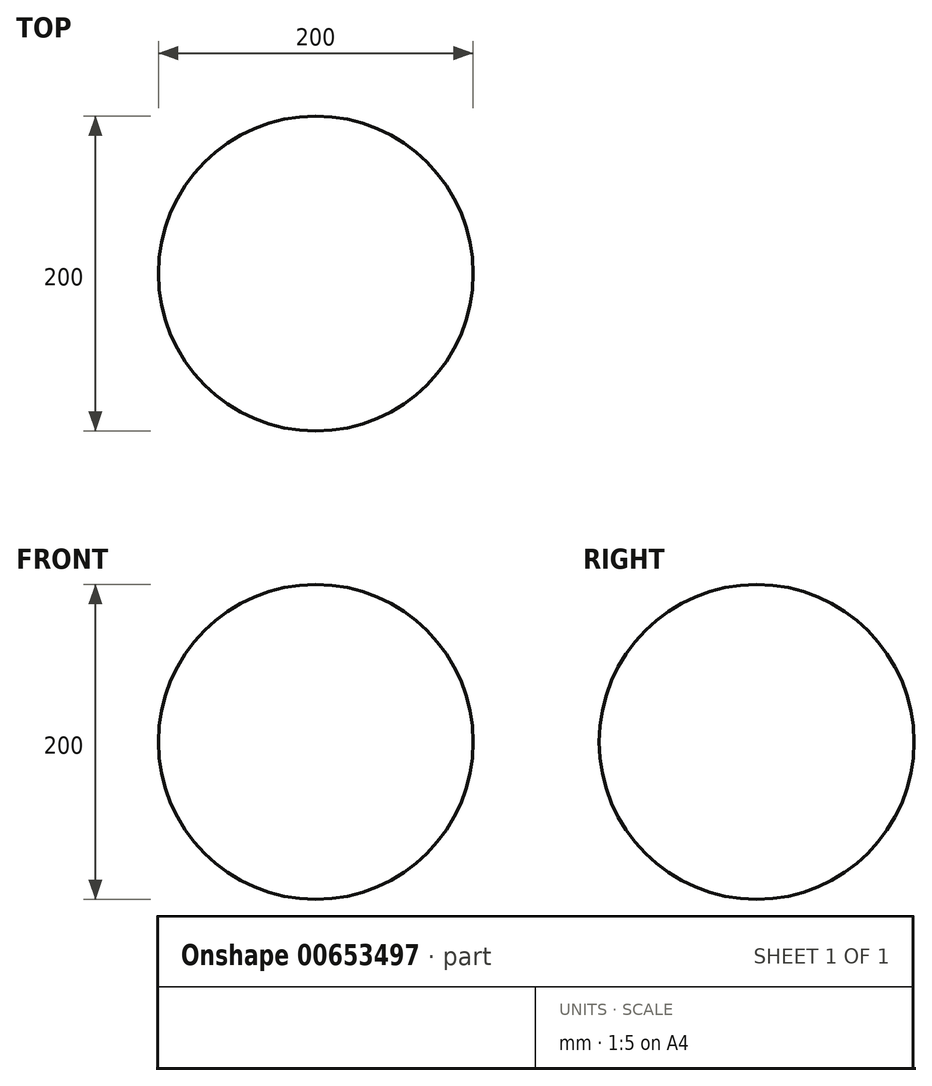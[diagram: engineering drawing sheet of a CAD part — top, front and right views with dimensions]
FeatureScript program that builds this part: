
annotation { "Feature Type Name" : "Feature", "Feature Type Description" : "" }
export const myFeature = defineFeature(function(context is Context, id is Id, definition is map)
    precondition{}
    {
        {
            var Q0;
            Q0=qCreatedBy(makeId("Front.planeOp"),FACE);
            var sketch = newSketch(context, id + "F0", { "sketchPlane" : qUnion([Q0])});
            skLineSegment(sketch, "E0.bottom", {"start": v(100, 100) * mm, "end": v(-100, 100) * mm});
            skLineSegment(sketch, "E0.top", {"start": v(100, -100) * mm, "end": v(-100, -100) * mm});
            skLineSegment(sketch, "E0.left", {"start": v(100, 100) * mm, "end": v(100, -100) * mm});
            skLineSegment(sketch, "E0.right", {"start": v(-100, 100) * mm, "end": v(-100, -100) * mm});
            skPoint(sketch, "E0.middle", {"position": v(0, 0) * mm});
            skSolve(sketch);
        }
        {
            var Q0;
            Q0=makeQuery(id+"F0.imprint","IMPRINT",FACE,{"disambiguationData":[TD([[makeQuery(id+"F0.imprint","IMPRINT",EDGE,{"derivedFrom":sQuery(id+"F0.wireOp",EDGE,"E0.bottom")}),1.0]])]});
            extrude(context, id + "F1", {"entities" : qUnion([Q0]), "depth" : 200 * mm, "offsetDistance" : 25 * mm});
        }
        {
            var Q0;
            Q0=makeQuery(id+"F1.opExtrude","SWEPT_FACE",FACE,{"disambiguationData":[OSD([sQuery(id+"F0.wireOp",EDGE,"E0.left")])]});
            var Q1;
            Q1=makeQuery(id+"F1.opExtrude","CAP_FACE",FACE,{"disambiguationData":[OSD([sQuery(id+"F0.wireOp",EDGE,"E0.bottom"),sQuery(id+"F0.wireOp",EDGE,"E0.top"),sQuery(id+"F0.wireOp",EDGE,"E0.left"),sQuery(id+"F0.wireOp",EDGE,"E0.right")])],"isStart":false});
            var Q2;
            Q2=makeQuery(id+"F1.opExtrude","SWEPT_FACE",FACE,{"disambiguationData":[OSD([sQuery(id+"F0.wireOp",EDGE,"E0.top")])]});
            var Q3;
            Q3=makeQuery(id+"F1.opExtrude","SWEPT_FACE",FACE,{"disambiguationData":[OSD([sQuery(id+"F0.wireOp",EDGE,"E0.right")])]});
            fillet(context, id + "F2", {"entities" : qUnion([Q0, Q1, Q2, Q3]), "radius" : 100 * mm, "tangentPropagation" : true, "allowEdgeOverflow" : false});
        }
        {
            var Q0;
            {var subQ0=sQuery(id+"F0.wireOp",EDGE,"E0.left");Q0=makeQuery(id+"F2.opFillet","BLEND_EDGE",EDGE,{"blendedFrom":[makeQuery(id+"F1.opExtrude","SWEPT_EDGE",EDGE,{"disambiguationData":[OSD([sQuery(id+"F0.wireOp",EDGE,"E0.bottom"),subQ0])]}),makeQuery(id+"F1.opExtrude","CAP_EDGE",EDGE,{"disambiguationData":[OSD([subQ0])],"isStart":true})],"blendedInto":[]});}
            fillet(context, id + "F3", {"entities" : qUnion([Q0]), "radius" : 100 * mm, "tangentPropagation" : true, "allowEdgeOverflow" : false});
        }
    });
